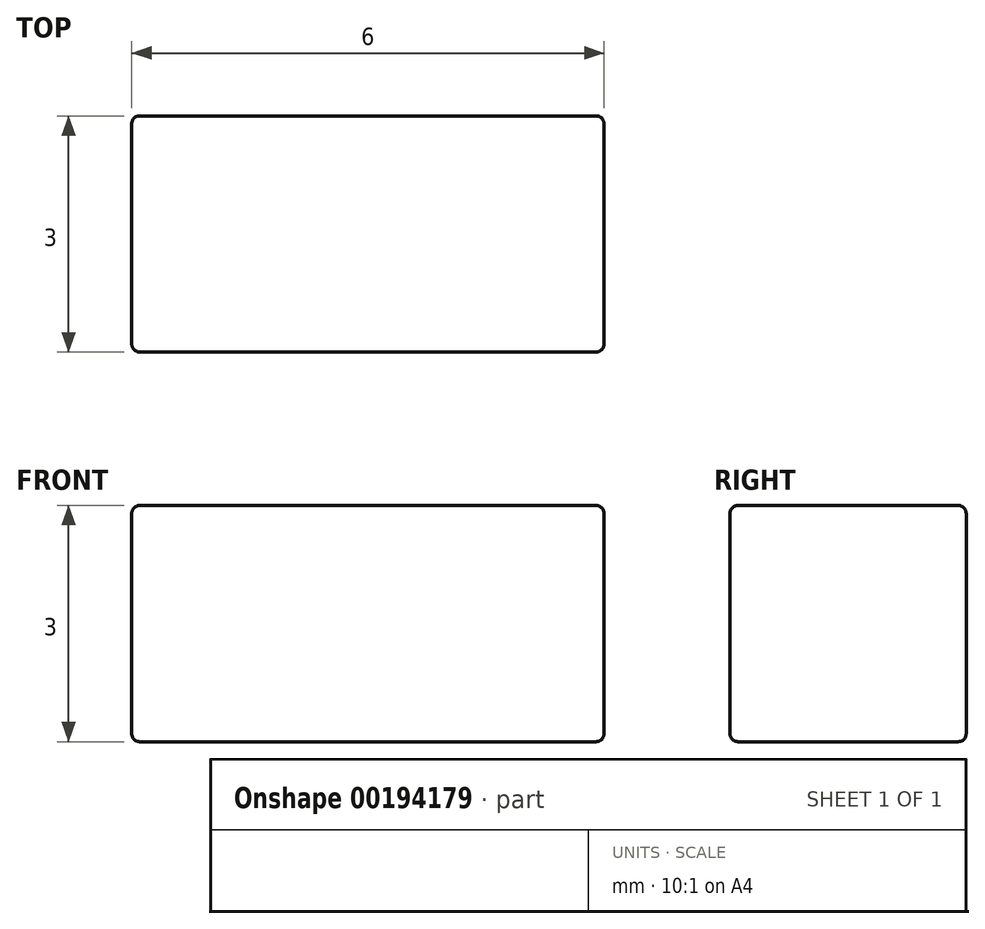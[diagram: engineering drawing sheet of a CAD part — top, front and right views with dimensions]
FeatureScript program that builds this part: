
annotation { "Feature Type Name" : "Feature", "Feature Type Description" : "" }
export const myFeature = defineFeature(function(context is Context, id is Id, definition is map)
    precondition{}
    {
        {
            var Q0;
            Q0=qCreatedBy(makeId("Top.planeOp"),FACE);
            var sketch = newSketch(context, id + "F0", { "sketchPlane" : qUnion([Q0])});
            skLineSegment(sketch, "E0.bottom", {"start": v(0, -1.5) * mm, "end": v(-3, -1.5) * mm});
            skLineSegment(sketch, "E0.top", {"start": v(0, 1.5) * mm, "end": v(-3, 1.5) * mm});
            skLineSegment(sketch, "E0.left", {"start": v(0, -1.5) * mm, "end": v(0, 1.5) * mm});
            skLineSegment(sketch, "E0.right", {"start": v(-3, -1.5) * mm, "end": v(-3, 1.5) * mm});
            skLineSegment(sketch, "E1.bottom", {"start": v(0, 1.5) * mm, "end": v(3, 1.5) * mm});
            skLineSegment(sketch, "E1.top", {"start": v(0, -1.5) * mm, "end": v(3, -1.5) * mm});
            skLineSegment(sketch, "E1.right", {"start": v(3, 1.5) * mm, "end": v(3, -1.5) * mm});
            skSolve(sketch);
        }
        {
            var Q0;
            Q0=makeQuery(id+"F0.imprint","IMPRINT",FACE,{"disambiguationData":[TD([[makeQuery(id+"F0.imprint","IMPRINT",EDGE,{"derivedFrom":sQuery(id+"F0.wireOp",EDGE,"E0.bottom")}),-1.0]])]});
            var Q1;
            Q1=makeQuery(id+"F0.imprint","IMPRINT",FACE,{"disambiguationData":[TD([[makeQuery(id+"F0.imprint","IMPRINT",EDGE,{"derivedFrom":sQuery(id+"F0.wireOp",EDGE,"E0.left")}),-1.0]])]});
            extrude(context, id + "F1", {"entities" : qUnion([Q0, Q1]), "depth" : 3 * mm, "symmetric" : true});
        }
        {
            var Q0;
            Q0=makeQuery(id+"F1.opExtrude","SWEPT_EDGE",EDGE,{"disambiguationData":[OSD([sQuery(id+"F0.wireOp",EDGE,"E1.bottom"),sQuery(id+"F0.wireOp",EDGE,"E1.right")])]});
            var Q1;
            Q1=makeQuery(id+"F1.opExtrude","SWEPT_EDGE",EDGE,{"disambiguationData":[OSD([sQuery(id+"F0.wireOp",EDGE,"E0.bottom"),sQuery(id+"F0.wireOp",EDGE,"E0.right")])]});
            var Q2;
            Q2=makeQuery(id+"F1.opExtrude","CAP_EDGE",EDGE,{"disambiguationData":[OSD([sQuery(id+"F0.wireOp",EDGE,"E0.right")])],"isStart":false});
            var Q3;
            Q3=makeQuery(id+"F1.opExtrude","CAP_EDGE",EDGE,{"disambiguationData":[OSD([sQuery(id+"F0.wireOp",EDGE,"E1.right")])],"isStart":true});
            var Q4;
            Q4=makeQuery(id+"F1.opExtrude","SWEPT_EDGE",EDGE,{"disambiguationData":[OSD([sQuery(id+"F0.wireOp",EDGE,"E1.top"),sQuery(id+"F0.wireOp",EDGE,"E1.right")])]});
            var Q5;
            Q5=makeQuery(id+"F1.opExtrude","CAP_EDGE",EDGE,{"disambiguationData":[OSD([sQuery(id+"F0.wireOp",EDGE,"E0.bottom"),sQuery(id+"F0.wireOp",EDGE,"E1.top")])],"isStart":true});
            var Q6;
            Q6=makeQuery(id+"F1.opExtrude","CAP_EDGE",EDGE,{"disambiguationData":[OSD([sQuery(id+"F0.wireOp",EDGE,"E0.bottom"),sQuery(id+"F0.wireOp",EDGE,"E1.top")])],"isStart":false});
            var Q7;
            Q7=makeQuery(id+"F1.opExtrude","CAP_EDGE",EDGE,{"disambiguationData":[OSD([sQuery(id+"F0.wireOp",EDGE,"E0.top"),sQuery(id+"F0.wireOp",EDGE,"E1.bottom")])],"isStart":false});
            var Q8;
            Q8=makeQuery(id+"F1.opExtrude","CAP_EDGE",EDGE,{"disambiguationData":[OSD([sQuery(id+"F0.wireOp",EDGE,"E1.right")])],"isStart":false});
            var Q9;
            Q9=makeQuery(id+"F1.opExtrude","SWEPT_EDGE",EDGE,{"disambiguationData":[OSD([sQuery(id+"F0.wireOp",EDGE,"E0.top"),sQuery(id+"F0.wireOp",EDGE,"E0.right")])]});
            var Q10;
            Q10=makeQuery(id+"F1.opExtrude","CAP_EDGE",EDGE,{"disambiguationData":[OSD([sQuery(id+"F0.wireOp",EDGE,"E0.right")])],"isStart":true});
            var Q11;
            Q11=makeQuery(id+"F1.opExtrude","CAP_EDGE",EDGE,{"disambiguationData":[OSD([sQuery(id+"F0.wireOp",EDGE,"E0.top"),sQuery(id+"F0.wireOp",EDGE,"E1.bottom")])],"isStart":true});
            fillet(context, id + "F2", {"entities" : qUnion([Q0, Q1, Q2, Q3, Q4, Q5, Q6, Q7, Q8, Q9, Q10, Q11]), "radius" : 0.1 * mm, "tangentPropagation" : true, "allowEdgeOverflow" : false});
        }
    });
